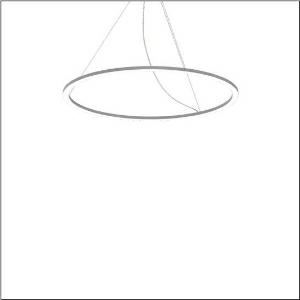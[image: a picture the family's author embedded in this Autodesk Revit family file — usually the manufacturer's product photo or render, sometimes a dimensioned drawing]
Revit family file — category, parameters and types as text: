
# Revit family: silica_21_ring-d_5pjbd3d3204a
name_source: partatom
category: Lighting Fixtures
units: mm (PartAtom-declared; Revit-internal decimal feet)

## family parameters
Cut with Voids When Loaded = No
Host = Face
Light Source = No
Part Type = Normal
Room Calculation Point = No
Round Connector Dimension = Use Diameter
Shared = No

## types (1)
- Silica 21 Ring-D (1 x LED, 8420 lm, 94 W, 4000K)
    Apparent Load = 94 VA
    CIE Flux Codes = 37 69 92 100 100
    Color Rendering = 80
    Color Temperature = 4000K
    Default Elevation = 1800 mm
    Description = Silica 21 Ring-D, suspended luminaire, of PMMA, frosted, light emission: ring underside luminous distribution, primary light characteristic: symmetric, installation type: suspended mounting, LED, rated luminous flux: 8.420lm, luminous efficacy: 90lm/W, light colour: 840, colour temperature: 4000K, control gear: DALI 2, with terminal, 5-pole, mains connection: 230V, AC/DC, 0/50..60Hz, rated input power: 94W, housing, of extruded aluminium section, metallic grey (RAL 9006), diameter: 1.100mm, ceiling canopy, metallic grey (RAL 9006), protection rating (lamp compartment): IP40, insulation class (complete): insulation class I (protective earthing), certification: CE, impact resistance: IK02, permissible operating ambient temperature: 0..+35°C, packaging unit: 1 piece
    Height = 25 mm  [stored 0.082021 ft]
    Lamp = 1 x LED
    Lamp Light Flux = 8420 lm
    Lamp Power = 94 W
    Lamp count = 1
    Length = 1100 mm
    Luminous efficacy = 90 lm/W
    Manufacturer = Siteco
    ModVariant = No
    Model = 5PJBD3D3204A
    Mounting Place = Ceiling
    Mounting Type = Pendant
    Number of Poles = 1
    OnlyDefault = Yes
    Power Factor = 1
    Product Name = Silica 21 Ring-D
    Product group = suspended luminaire
    ProductGroupID = 904
    Protection Class = Protection class I
    Protection Degree = IP 40
    RLX_Detail_Level = 1
    RLX_Emergency_Light_Flux = 0 lm
    RLX_Emergency_Type = 0
    RLX_Emergency_Type_DB = No
    RlxData = <blob elided: 14565 chars, md5=3fbbcf01>
    Socket = socket
    Standby Power = 0 W
    System Light Flux = 8420 lm
    System Power = 94 W
    Type Comments = Product without accessories
    Type Image = l_1251746.jpg
    URL = http://relux.com
    VarID = ---
    Voltage = 0 V
    Weight = 0.00 kg
    Width = 0 mm  [stored 0 ft]

note: [stored X ft] marks values corroborated as IEEE doubles in the binary element streams (Revit-internal decimal feet)

## geometry (parser evidence)
native form markers: Sweep x12
no freeform markers — native parametric forms only
